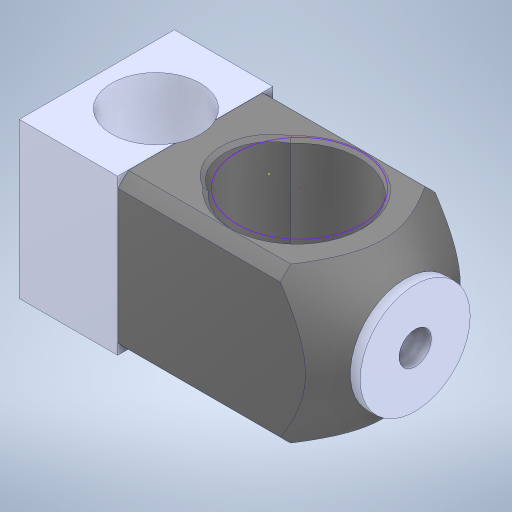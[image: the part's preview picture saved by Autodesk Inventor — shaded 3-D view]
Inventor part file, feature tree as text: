
AUTODESK INVENTOR PART (.ipt)
format: ipt  version: 2023 (Build 270158000, 158)  size: 342,016 bytes
history: mixed  units: in
note: dims shown in document units (in); Inventor stores cm internally (conversion verified against a paired STEP export)
features: sketch x8, extrude x7, other x1, imported_body x1
ambient origin geometry x8: Origin, YZ Plane, XZ Plane, XY Plane, X Axis, Y Axis, Z Axis, Center Point
bodies: Solid1 (imported_parasolid)
feature tree (17):
  other  "6669-001-1-solid1"
  extrude  "Extrusion1"  Depth=0.3937in
  sketch  "Sketch2"  dims[d8=0.3937in d9=0.0in d10=0.0in d11=0.0in]
  extrude  "Extrusion4"  TaperAngle=0.0deg  [1 undecoded]
  sketch  "Sketch5"  dims[d16=0.2362in d17=0.1969in]
  extrude  "Extrusion5"  Depth=0.3937in TaperAngle=0.0deg
  extrude  "Extrusion6"  Depth=0.1969in
  extrude  "Extrusion7"  Depth=0.3543in
  extrude  "Extrusion8"  Depth=0.0197in
  extrude  "Extrusion9"  Depth=0.0197in
  sketch  "Sketch1"  dims[d0=0.3937in d1=0.0in d7=0.1299in]
  sketch  "Sketch4"  dims[d12=0.0394in d13=0.0in d14=0.3937in d15=0.0in]
  sketch  "Sketch6"  dims[d18=0.1969in d19=0.0in d20=0.3543in]
  sketch  "Sketch7"  dims[d21=0.0in d22=0.0in d2=0.0197in]
  sketch  "Sketch8"  dims[d3=0.0344in d4=0.0197in]
  sketch  "Sketch9"  dims[d5=0.0344in]
  imported_body  NMx_Import_Brep_tag  [imported B-rep: ~14 faces, bbox_mm=[22.836, 10.765997, 12.379599]]
note: 1 required parameter value undecoded (feature->parameter linkage not recoverable at this tier; creation-order binding heuristic only, values carry confidence <= 0.55)
